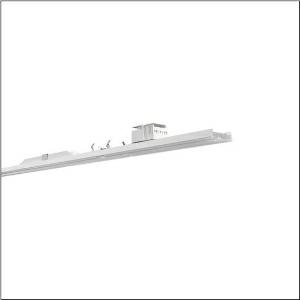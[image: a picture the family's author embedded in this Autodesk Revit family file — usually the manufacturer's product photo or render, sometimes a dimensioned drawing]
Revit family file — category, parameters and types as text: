
# Revit family: licross_r__11_recessed_mo_51tl18vn565f_cd8b
name_source: partatom
category: Lighting Fixtures
units: mm (PartAtom-declared; Revit-internal decimal feet)

## family parameters
Cut with Voids When Loaded = No
Host = Face
Light Source = No
Part Type = Normal
Room Calculation Point = No
Round Connector Dimension = Use Diameter
Shared = No

## types (1)
- --- (1 x LED, 6530 lm, 39.6 W, 5000K)
    Apparent Load = 40 VA
    CIE Flux Codes = 83 96 99 100 100
    Color Rendering = 80
    Color Temperature = 5000K
    Default Elevation = 1800 mm
    Description = Licross® 11 Recessed MOluminaire insert, length: 1.500mm, width: 66mm, height: 67mm, LED rated luminous flux: 6.530lm, light colour: 850, control gear: DALI 2, CLO, control gear: ECG DALI, with plug, 5-pole, with phase selection, mains connection: 220..240V, AC, 50/60Hz, halogen-free wiring, primary optical cover: cover, of PMMA, light emission: direct distribution, protection rating (complete): IP40, insulation class (complete): insulation class I (protective earthing), certification: CE, ENEC, VDE, UKCA, protection symbol: D if used in an environment without relevant dust loads with corresponding accessories, permissible ambient temperature for indoor applications: -25..+40°C, corresponds to IFS (International Featured Standards) requirements for safety and quality in the food industry, reducing of maximum allowable ambient temperature of 5°C with ceiling mounting, packaging unit: 1 piece
    Height = 58 mm
    Lamp = 1 x LED
    Lamp Light Flux = 6530 lm
    Lamp Power = 39.6 W
    Lamp count = 1
    Length = 1500 mm
    Luminous efficacy = 165 lm/W
    Manufacturer = Siteco
    ModVariant = No
    Model = 51TL18VN565F
    Mounting Place = Ceiling
    Mounting Type = Pendant
    Number of Poles = 1
    OnlyDefault = Yes
    Power Factor = 1
    Product Name = Licross® 11 Recessed MO
    Product group = luminaire insert
    ProductGroupID = 902
    Protection Class = Protection class I
    Protection Degree = IP 40
    RLX_Detail_Level = 1
    RlxData = <blob elided: 22325 chars, md5=23cb4312>
    Socket = socket
    Standby Power = 0 W
    System Light Flux = 6530 lm
    System Power = 40 W
    Type Comments = factory setting: luminous flux: 100 % | dim-lin: 254 | 261 mA
    Type Image = l_1266722.jpg
    URL = http://relux.com
    VarID = @adj_128945
    Voltage = 0 V
    Weight = 0.00 kg
    Width = 66 mm

## geometry (parser evidence)
native form markers: Blend x4, Sweep x10
no freeform markers — native parametric forms only
